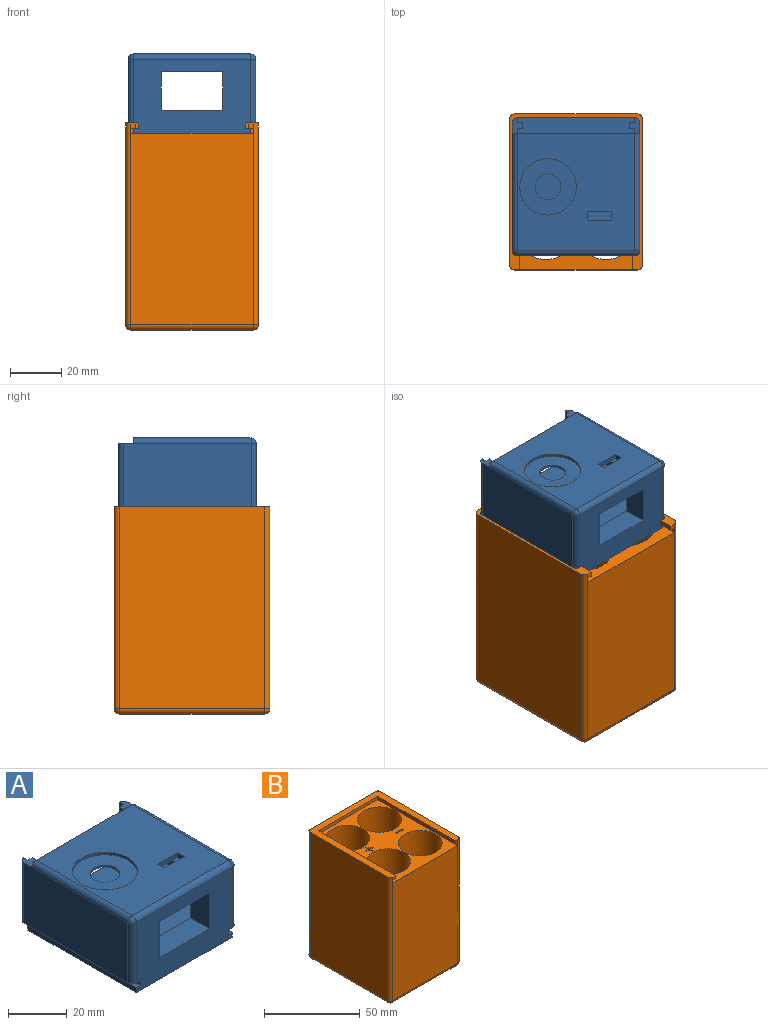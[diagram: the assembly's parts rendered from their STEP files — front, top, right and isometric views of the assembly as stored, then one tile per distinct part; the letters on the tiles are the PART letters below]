
ASSEMBLY  parts=2 mates=1
PART A: 82 faces, bbox 50x54x31 mm
  f0: plane 46x46mm, normal (0,0,-1), area 1994.7mm2, adj f2,f10,f11,f31,f34,f72,f73,f74
  f1: plane 46x46mm, normal (0,0,1), area 1701.1mm2, adj f31,f32,f46,f47,f51,f72,f73,f74
  f2: plane 46x23mm, normal (0,1,0), area 412mm2, adj f0,f7,f10,f11,f63,f64,f65,f66
  f3: plane 46x29mm, normal (0,-1,0), area 966mm2, adj f6,f13,f15,f16,f18,f19,f20,f45
  f4: plane 10x5.5mm, normal (0,1,0), area 55mm2, adj f7,f35,f37,f44
  f5: plane 10x5.5mm, normal (0,1,0), area 55mm2, adj f7,f38,f40,f42
  f6: plane 52x46mm, normal (0,0,-1), area 1752mm2, adj f3,f13,f14,f15,f35,f36,f37,f38
  f7: plane 52x46mm, normal (0,0,1), area 2364mm2, adj f2,f4,f5,f10,f11,f12,f23,f24
  f8: plane 6x4mm, normal (0,0,1), area 15.1mm2, adj f11,f22,f23,f25,f26,f27,f31,f53
  f9: plane 6x4mm, normal (0,0,1), area 15.1mm2, adj f10,f21,f24,f28,f29,f30,f31,f52
  f10: plane 48x23mm, normal (-1,0,0), area 927.3mm2, adj f0,f2,f7,f9,f29,f58
  f11: plane 48x23mm, normal (1,0,0), area 1104mm2, adj f0,f2,f7,f8,f26
  f12: plane 46x2mm, normal (0,1,0), area 92mm2, adj f7,f20,f52,f53
  f13: plane 52x2mm, normal (1,0,0), area 104mm2, adj f3,f6,f14,f16
  f14: plane 46x2mm, normal (0,1,0), area 92mm2, adj f6,f13,f15,f16
  f15: plane 52x2mm, normal (-1,0,0), area 104mm2, adj f3,f6,f14,f16
  f16: plane 52x46mm, normal (0,0,1), area 292mm2, adj f3,f13,f14,f15,f17,f18,f19
  f17: plane 42x2mm, normal (0,1,0), area 84mm2, adj f16,f18,f19,f20
  f18: plane 50x2mm, normal (-1,0,0), area 100mm2, adj f3,f16,f17,f20
  f19: plane 50x2mm, normal (1,0,0), area 100mm2, adj f3,f16,f17,f20
  f20: plane 54x50mm, normal (0,0,-1), area 596.6mm2, adj f3,f12,f17,f18,f19,f21,f22,f45
  f21: plane 50x25mm, normal (1,0,0), area 1136.9mm2, adj f9,f20,f47,f48,f52,f60
  f22: plane 50x25mm, normal (-1,0,0), area 1250mm2, adj f8,f20,f45,f46,f53
  f23: plane 23x2mm, normal (1,0,0), area 46mm2, adj f7,f8,f25,f53
  f24: plane 23x2mm, normal (-1,0,0), area 46mm2, adj f7,f9,f28,f52
  f25: plane 23x2mm, normal (0,1,0), area 46mm2, adj f7,f8,f23,f27
  f26: plane 23x2mm, normal (0,-1,0), area 46mm2, adj f7,f8,f11,f27
  f27: plane 23x2mm, normal (1,0,0), area 46mm2, adj f7,f8,f25,f26
  f28: plane 23x2mm, normal (0,1,0), area 46mm2, adj f7,f9,f24,f30
  f29: plane 23x2mm, normal (0,-1,0), area 46mm2, adj f7,f9,f10,f30
  f30: plane 23x2mm, normal (-1,0,0), area 46mm2, adj f7,f9,f28,f29
  f31: plane 50x2mm, normal (0,1,0), area 98.3mm2, adj f0,f1,f8,f9,f46,f47
  f32: cylinder r=11.05mm len=22.1mm, axis (0,0,1), area 76.4mm2, adj f1,f33
  f33: plane 22.1x22.1mm, normal (0,0,1), area 303.5mm2, adj f32,f34
  f34: cylinder r=5.05mm len=10.1mm, axis (0,0,1), area 28.6mm2, adj f0,f33
  f35: plane 32x6mm, normal (-1,0,0), area 21.5mm2, adj f4,f6,f7,f36,f43,f44
  f36: plane 10x6mm, normal (0,-1,0), area 60mm2, adj f6,f7,f35,f37
  f37: plane 32x6mm, normal (1,0,0), area 21.5mm2, adj f4,f6,f7,f36,f43,f44
  f38: plane 32x6mm, normal (-1,0,0), area 21.5mm2, adj f5,f6,f7,f39,f41,f42
  f39: plane 10x6mm, normal (0,-1,0), area 60mm2, adj f6,f7,f38,f40
  f40: plane 32x6mm, normal (1,0,0), area 21.5mm2, adj f5,f6,f7,f39,f41,f42
  f41: plane 10x0.5mm, normal (0,1,0), area 5mm2, adj f6,f38,f40,f42
  f42: plane 31x10mm, normal (0,0,-1), area 310mm2, adj f5,f38,f40,f41
  f43: plane 10x0.5mm, normal (0,1,0), area 5mm2, adj f6,f35,f37,f44
  f44: plane 31x10mm, normal (0,0,-1), area 310mm2, adj f4,f35,f37,f43
  f45: cylinder r=2mm len=25mm, axis (0,0,1), area 78.5mm2, adj f3,f20,f22,f49
  f46: cylinder r=2mm len=46mm, axis (0,1,0), area 144.5mm2, adj f1,f22,f31,f49
  f47: cylinder r=2mm len=46mm, axis (0,-1,0), area 144.5mm2, adj f1,f21,f31,f50
  f48: cylinder r=2mm len=25mm, axis (0,0,-1), area 78.5mm2, adj f3,f20,f21,f50
  f49: sphere r=2mm, area 6.3mm2, adj f45,f46,f51
  f50: sphere r=2mm, area 6.3mm2, adj f47,f48,f51
  f51: cylinder r=2mm len=46mm, axis (-1,0,0), area 144.5mm2, adj f1,f3,f49,f50
  f52: cylinder r=2mm len=25mm, axis (0,0,1), area 78.5mm2, adj f9,f12,f20,f21,f24
  f53: cylinder r=2mm len=25mm, axis (0,0,-1), area 78.5mm2, adj f8,f12,f20,f22,f23
  f54: plane 24x9mm, normal (0,0,-1), area 216mm2, adj f3,f55,f57,f67
  f55: plane 15x9mm, normal (1,0,0), area 135mm2, adj f3,f54,f56,f67
  f56: plane 24x9mm, normal (0,0,1), area 216mm2, adj f3,f55,f57,f67
  f57: plane 15x9mm, normal (-1,0,0), area 135mm2, adj f3,f54,f56,f67
  f58: cylinder r=7.5mm len=15mm, axis (1,0,0), area 282.7mm2, adj f10,f59
  f59: plane 15x15mm, normal (-1,0,0), area 136mm2, adj f58,f62
  f60: cylinder r=6mm len=12mm, axis (1,0,0), area 226.2mm2, adj f21,f61
  f61: plane 12x12mm, normal (1,0,0), area 72.4mm2, adj f60,f62
  f62: cylinder r=3.6mm len=7.2mm, axis (-1,0,0), area 45.2mm2, adj f59,f61
  f63: plane 34x7mm, normal (0,0,1), area 238mm2, adj f2,f64,f66,f67
  f64: plane 19x7mm, normal (1,0,0), area 133mm2, adj f2,f63,f65,f67
  f65: plane 34x7mm, normal (0,0,-1), area 238mm2, adj f2,f64,f66,f67
  f66: plane 19x7mm, normal (-1,0,0), area 133mm2, adj f2,f63,f65,f67
  f67: plane 34x19mm, normal (0,1,0), area 279.7mm2, adj f54,f55,f56,f57,f63,f64,f65,f66
  f68: cylinder r=1mm len=4mm, axis (0,1,0), area 25.1mm2, adj f67,f69
  f69: plane 2x2mm, normal (0,1,0), area 3.1mm2, adj f68
  f70: cylinder r=1mm len=4mm, axis (0,1,0), area 25.1mm2, adj f67,f71
  f71: plane 2x2mm, normal (0,1,0), area 3.1mm2, adj f70
  f72: plane 9.5x2mm, normal (0,1,0), area 19mm2, adj f0,f1,f73,f75
  f73: plane 3.3x2mm, normal (-1,0,0), area 6.6mm2, adj f0,f1,f72,f74
  f74: plane 9.5x2mm, normal (0,-1,0), area 19mm2, adj f0,f1,f73,f75
  f75: plane 3.3x2mm, normal (1,0,0), area 6.6mm2, adj f0,f1,f72,f74
  f76: cylinder r=1.25mm len=2.5mm, axis (0,0,1), area 15.7mm2, adj f0,f81
  f77: plane 0.5x0.5mm, normal (0,0,-1), area 0.2mm2, adj f81
  f78: cylinder r=1.25mm len=2.5mm, axis (0,0,1), area 15.7mm2, adj f0,f80
  f79: plane 0.5x0.5mm, normal (0,0,-1), area 0.2mm2, adj f80
  f80: torus R=0.25mm, axis (0,0,-1), area 8.8mm2, adj f78,f79
  f81: torus R=0.25mm, axis (0,0,-1), area 8.8mm2, adj f76,f77
PART B: 106 faces, bbox 52x61x81 mm
  f0: plane 2x2mm, normal (0,-1,0), area 4mm2, adj f31,f32,f33,f95
  f1: plane 75x48mm, normal (0,-1,0), area 3600mm2, adj f4,f92,f95,f96
  f2: plane 48x2mm, normal (0,0,-1), area 96mm2, adj f22,f93,f96,f99
  f3: plane 48x5mm, normal (0,0,-1), area 240mm2, adj f24,f26,f99,f105
  f4: plane 59x48mm, normal (0,0,1), area 1156.1mm2, adj f1,f7,f16,f17,f18,f19,f29,f30
  f5: plane 50x27.25mm, normal (0,0,-1), area 523.5mm2, adj f8,f9,f15,f18,f19,f37,f56,f57
  f6: plane 50x27.75mm, normal (0,0,-1), area 548.5mm2, adj f10,f11,f15,f16,f17,f36,f38,f39
  f7: plane 48x2mm, normal (0,-1,0), area 96mm2, adj f4,f29,f30,f32
  f8: plane 50x2mm, normal (0,-1,0), area 100mm2, adj f5,f27,f37,f101
  f9: plane 50x2mm, normal (0,1,0), area 100mm2, adj f5,f15,f25,f37
  f10: plane 50x2mm, normal (0,-1,0), area 100mm2, adj f6,f15,f23,f36
  f11: plane 50x2mm, normal (0,1,0), area 100mm2, adj f6,f21,f36,f92
  f12: plane 79x48mm, normal (0,1,0), area 3792mm2, adj f31,f98,f101,f104
  f13: plane 79x57mm, normal (-1,0,0), area 4503mm2, adj f31,f95,f98,f99
  f14: plane 2x2mm, normal (0,-1,0), area 4mm2, adj f31,f32,f34,f92
  f15: plane 79x57mm, normal (1,0,0), area 4393mm2, adj f5,f6,f9,f10,f31,f92,f101,f105
  f16: cylinder r=11.5mm len=73mm, axis (0,0,-1), area 5274.7mm2, adj f4,f6
  f17: cylinder r=11.5mm len=73mm, axis (0,0,-1), area 5274.7mm2, adj f4,f6
  f18: cylinder r=11.5mm len=73mm, axis (0,0,-1), area 5274.7mm2, adj f4,f5
  f19: cylinder r=11.5mm len=73mm, axis (0,0,-1), area 5274.7mm2, adj f4,f5
  f20: plane 48x2mm, normal (0,0,-1), area 96mm2, adj f28,f99,f100,f104
  f21: plane 50x2mm, normal (0,0,1), area 100mm2, adj f11,f22,f36,f93
  f22: plane 50x2mm, normal (0,1,0), area 99.1mm2, adj f2,f21,f36,f93
  f23: plane 50x1.75mm, normal (0,0,1), area 87.5mm2, adj f10,f24,f36,f105
  f24: plane 50x2mm, normal (0,-1,0), area 99.1mm2, adj f3,f23,f36,f105
  f25: plane 50x1.25mm, normal (0,0,1), area 62.5mm2, adj f9,f26,f37,f105
  f26: plane 50x2mm, normal (0,1,0), area 99.1mm2, adj f3,f25,f37,f105
  f27: plane 50x2mm, normal (0,0,1), area 100mm2, adj f8,f28,f37,f100
  f28: plane 50x2mm, normal (0,-1,0), area 99.1mm2, adj f20,f27,f37,f100
  f29: plane 59x2mm, normal (1,0,0), area 118mm2, adj f4,f7,f32,f95
  f30: plane 59x2mm, normal (-1,0,0), area 118mm2, adj f4,f7,f32,f92
  f31: plane 61x52mm, normal (0,0,1), area 660.6mm2, adj f0,f12,f13,f14,f15,f33,f34,f35
  f32: plane 59x48mm, normal (0,0,-1), area 324mm2, adj f0,f7,f14,f29,f30,f33,f34,f35
  f33: plane 57x2mm, normal (1,0,0), area 114mm2, adj f0,f31,f32,f35
  f34: plane 57x2mm, normal (-1,0,0), area 114mm2, adj f14,f31,f32,f35
  f35: plane 44x2mm, normal (0,-1,0), area 88mm2, adj f31,f32,f33,f34
  f36: plane 27.75x4mm, normal (1,0,0), area 103.5mm2, adj f6,f10,f11,f21,f22,f23,f24,f99
  f37: plane 27.25x4mm, normal (1,0,0), area 102.5mm2, adj f5,f8,f9,f25,f26,f27,f28,f99
  f38: plane 1.5x1mm, normal (0,1,0), area 1.5mm2, adj f6,f39,f49,f50
  f39: plane 1.5x1mm, normal (1,0,0), area 1.5mm2, adj f6,f38,f40,f50
  f40: plane 1.5x1mm, normal (0,1,0), area 1.5mm2, adj f6,f39,f41,f50
  f41: plane 1.5x1mm, normal (1,0,0), area 1.5mm2, adj f6,f40,f42,f50
  f42: plane 1.5x1mm, normal (0,-1,0), area 1.5mm2, adj f6,f41,f43,f50
  f43: plane 1.5x1mm, normal (1,0,0), area 1.5mm2, adj f6,f42,f44,f50
  f44: plane 1.5x1mm, normal (0,-1,0), area 1.5mm2, adj f6,f43,f45,f50
  f45: plane 1.5x1mm, normal (-1,0,0), area 1.5mm2, adj f6,f44,f46,f50
  f46: plane 1.5x1mm, normal (0,-1,0), area 1.5mm2, adj f6,f45,f47,f50
  f47: plane 1.5x1mm, normal (-1,0,0), area 1.5mm2, adj f6,f46,f48,f50
  f48: plane 1.5x1mm, normal (0,1,0), area 1.5mm2, adj f6,f47,f49,f50
  f49: plane 1.5x1mm, normal (-1,0,0), area 1.5mm2, adj f6,f38,f48,f50
  f50: plane 3x3mm, normal (0,0,-1), area 5mm2, adj f38,f39,f40,f41,f42,f43,f44,f45
  f51: plane 3x1.5mm, normal (0,1,0), area 4.5mm2, adj f6,f52,f54,f55
  f52: plane 1.5x1mm, normal (1,0,0), area 1.5mm2, adj f6,f51,f53,f55
  f53: plane 3x1.5mm, normal (0,-1,0), area 4.5mm2, adj f6,f52,f54,f55
  f54: plane 1.5x1mm, normal (-1,0,0), area 1.5mm2, adj f6,f51,f53,f55
  f55: plane 3x1mm, normal (0,0,-1), area 3mm2, adj f51,f52,f53,f54
  f56: plane 1.5x1mm, normal (0,1,0), area 1.5mm2, adj f5,f57,f67,f68
  f57: plane 1.5x1mm, normal (1,0,0), area 1.5mm2, adj f5,f56,f58,f68
  f58: plane 1.5x1mm, normal (0,1,0), area 1.5mm2, adj f5,f57,f59,f68
  f59: plane 1.5x1mm, normal (1,0,0), area 1.5mm2, adj f5,f58,f60,f68
  f60: plane 1.5x1mm, normal (0,-1,0), area 1.5mm2, adj f5,f59,f61,f68
  f61: plane 1.5x1mm, normal (1,0,0), area 1.5mm2, adj f5,f60,f62,f68
  f62: plane 1.5x1mm, normal (0,-1,0), area 1.5mm2, adj f5,f61,f63,f68
  f63: plane 1.5x1mm, normal (-1,0,0), area 1.5mm2, adj f5,f62,f64,f68
  f64: plane 1.5x1mm, normal (0,-1,0), area 1.5mm2, adj f5,f63,f65,f68
  f65: plane 1.5x1mm, normal (-1,0,0), area 1.5mm2, adj f5,f64,f66,f68
  f66: plane 1.5x1mm, normal (0,1,0), area 1.5mm2, adj f5,f65,f67,f68
  f67: plane 1.5x1mm, normal (-1,0,0), area 1.5mm2, adj f5,f56,f66,f68
  f68: plane 3x3mm, normal (0,0,-1), area 5mm2, adj f56,f57,f58,f59,f60,f61,f62,f63
  f69: plane 3x1.5mm, normal (0,1,0), area 4.5mm2, adj f5,f70,f72,f73
  f70: plane 1.5x1mm, normal (1,0,0), area 1.5mm2, adj f5,f69,f71,f73
  f71: plane 3x1.5mm, normal (0,-1,0), area 4.5mm2, adj f5,f70,f72,f73
  f72: plane 1.5x1mm, normal (-1,0,0), area 1.5mm2, adj f5,f69,f71,f73
  f73: plane 3x1mm, normal (0,0,-1), area 3mm2, adj f69,f70,f71,f72
  f74: plane 5x1.5mm, normal (0,-1,0), area 7.5mm2, adj f4,f75,f77,f78
  f75: plane 1.5x1mm, normal (1,0,0), area 1.5mm2, adj f4,f74,f76,f78
  f76: plane 5x1.5mm, normal (0,1,0), area 7.5mm2, adj f4,f75,f77,f78
  f77: plane 1.5x1mm, normal (-1,0,0), area 1.5mm2, adj f4,f74,f76,f78
  f78: plane 5x1mm, normal (0,0,1), area 5mm2, adj f74,f75,f76,f77
  f79: plane 2x1.5mm, normal (-1,0,0), area 3mm2, adj f4,f80,f90,f91
  f80: plane 2x1.5mm, normal (0,1,0), area 3mm2, adj f4,f79,f81,f91
  f81: plane 1.5x1mm, normal (-1,0,0), area 1.5mm2, adj f4,f80,f82,f91
  f82: plane 2x1.5mm, normal (0,-1,0), area 3mm2, adj f4,f81,f83,f91
  f83: plane 2x1.5mm, normal (-1,0,0), area 3mm2, adj f4,f82,f84,f91
  f84: plane 1.5x1mm, normal (0,-1,0), area 1.5mm2, adj f4,f83,f85,f91
  f85: plane 2x1.5mm, normal (1,0,0), area 3mm2, adj f4,f84,f86,f91
  f86: plane 2x1.5mm, normal (0,-1,0), area 3mm2, adj f4,f85,f87,f91
  f87: plane 1.5x1mm, normal (1,0,0), area 1.5mm2, adj f4,f86,f88,f91
  f88: plane 2x1.5mm, normal (0,1,0), area 3mm2, adj f4,f87,f89,f91
  f89: plane 2x1.5mm, normal (1,0,0), area 3mm2, adj f4,f88,f90,f91
  f90: plane 1.5x1mm, normal (0,1,0), area 1.5mm2, adj f4,f79,f89,f91
  f91: plane 5x5mm, normal (0,0,1), area 9mm2, adj f79,f80,f81,f82,f83,f84,f85,f86
  f92: cylinder r=2mm len=79mm, axis (0,0,1), area 248.2mm2, adj f1,f11,f14,f15,f30,f31,f94
  f93: cylinder r=2mm len=2mm, axis (0,-1,0), area 6.3mm2, adj f2,f21,f22,f94
  f94: sphere r=2mm, area 6.3mm2, adj f92,f93,f96
  f95: cylinder r=2mm len=79mm, axis (0,0,-1), area 248.2mm2, adj f0,f1,f13,f29,f31,f97
  f96: cylinder r=2mm len=48mm, axis (-1,0,0), area 150.8mm2, adj f1,f2,f94,f97
  f97: sphere r=2mm, area 6.3mm2, adj f95,f96,f99
  f98: cylinder r=2mm len=79mm, axis (0,0,1), area 248.2mm2, adj f12,f13,f31,f102
  f99: cylinder r=2mm len=57mm, axis (0,1,0), area 179.1mm2, adj f2,f3,f13,f20,f36,f37,f97,f102
  f100: cylinder r=2mm len=2mm, axis (0,-1,0), area 6.3mm2, adj f20,f27,f28,f103
  f101: cylinder r=2mm len=79mm, axis (0,0,-1), area 248.2mm2, adj f8,f12,f15,f31,f103
  f102: sphere r=2mm, area 6.3mm2, adj f98,f99,f104
  f103: sphere r=2mm, area 6.3mm2, adj f100,f101,f104
  f104: cylinder r=2mm len=48mm, axis (1,0,0), area 150.8mm2, adj f12,f20,f102,f103
  f105: cylinder r=2mm len=5mm, axis (0,-1,0), area 15.7mm2, adj f3,f15,f23,f24,f25,f26
PLACE A t=(-33.65,2.56,65.81)mm
PLACE B t=(-33.68,1.65,-7.19)mm
MATE fastened A.f6 <-> B.f4  axis (0,0,-1) through (-33.65,2.2,65.81)mm
